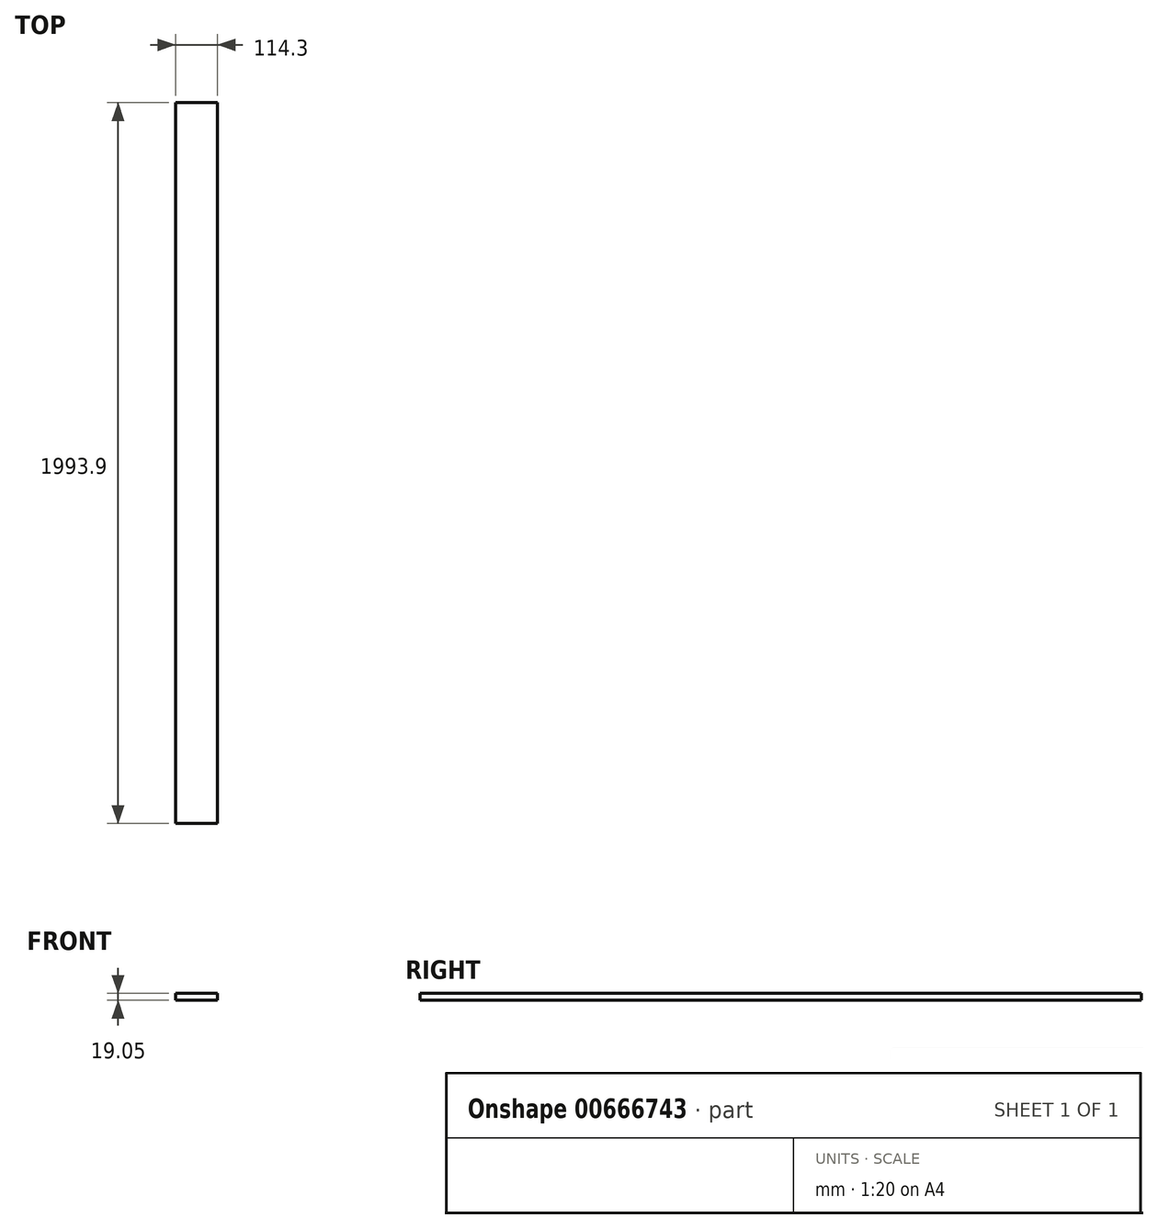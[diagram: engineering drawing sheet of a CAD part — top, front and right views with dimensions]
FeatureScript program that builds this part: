
annotation { "Feature Type Name" : "Feature", "Feature Type Description" : "" }
export const myFeature = defineFeature(function(context is Context, id is Id, definition is map)
    precondition{}
    {
        {
            var Q0;
            Q0=qCreatedBy(makeId("Top.planeOp"),FACE);
            var sketch = newSketch(context, id + "F0", { "sketchPlane" : qUnion([Q0])});
            skLineSegment(sketch, "E0.bottom", {"start": v(57.15, 996.95) * mm, "end": v(-57.15, 996.95) * mm});
            skLineSegment(sketch, "E0.top", {"start": v(57.15, -996.95) * mm, "end": v(-57.15, -996.95) * mm});
            skLineSegment(sketch, "E0.left", {"start": v(57.15, 996.95) * mm, "end": v(57.15, -996.95) * mm});
            skLineSegment(sketch, "E0.right", {"start": v(-57.15, 996.95) * mm, "end": v(-57.15, -996.95) * mm});
            skPoint(sketch, "E0.middle", {"position": v(0, 0) * mm});
            skSolve(sketch);
        }
        {
            var Q0;
            Q0=makeQuery(id+"F0.imprint","IMPRINT",FACE,{"disambiguationData":[TD([[makeQuery(id+"F0.imprint","IMPRINT",EDGE,{"derivedFrom":sQuery(id+"F0.wireOp",EDGE,"E0.bottom")}),1.0]])]});
            extrude(context, id + "F1", {"entities" : qUnion([Q0]), "depth" : 19.05 * mm, "offsetDistance" : 25.4 * mm});
        }
    });
